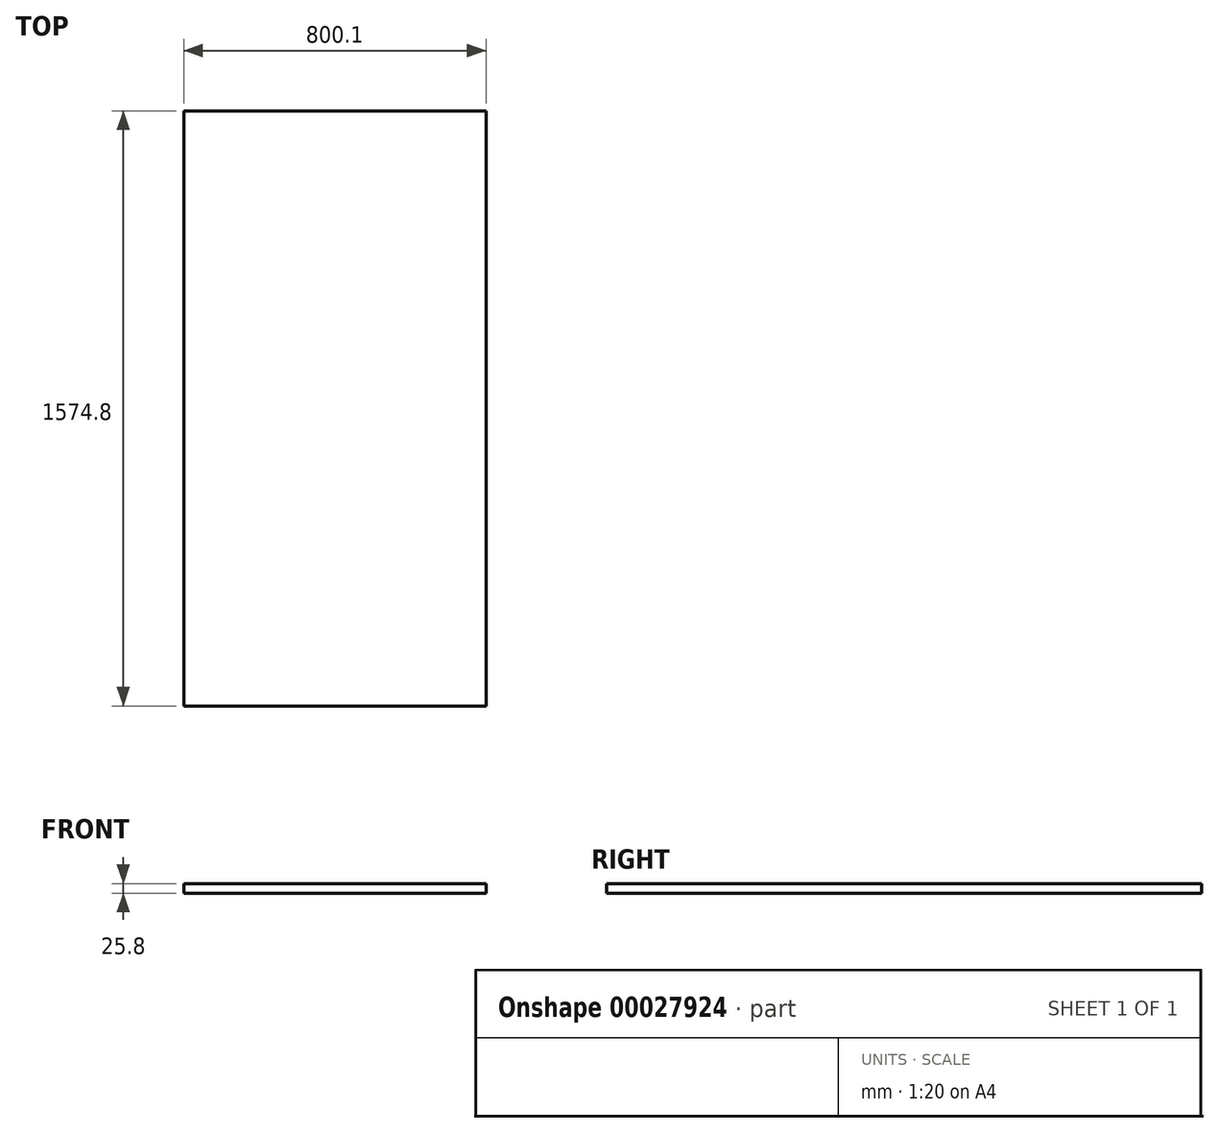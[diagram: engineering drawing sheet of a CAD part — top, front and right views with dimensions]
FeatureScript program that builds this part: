
annotation { "Feature Type Name" : "Feature", "Feature Type Description" : "" }
export const myFeature = defineFeature(function(context is Context, id is Id, definition is map)
    precondition{}
    {
        {
            var Q0;
            Q0=qCreatedBy(makeId("Front.planeOp"),FACE);
            var sketch = newSketch(context, id + "F0", { "sketchPlane" : qUnion([Q0])});
            skLineSegment(sketch, "E0", {"start": v(0, 0) * mm, "end": v(800.1, 0) * mm});
            skLineSegment(sketch, "E1", {"start": v(800.1, 0) * mm, "end": v(800.1, 25.8) * mm});
            skLineSegment(sketch, "E2", {"start": v(800.1, 25.8) * mm, "end": v(0, 25.8) * mm});
            skLineSegment(sketch, "E3", {"start": v(0, 25.8) * mm, "end": v(0, 0) * mm});
            skSolve(sketch);
        }
        {
            var Q0;
            Q0=qSketchRegion(id+"F0",true);
            extrude(context, id + "F1", {"entities" : qUnion([Q0]), "depth" : 1574.8 * mm});
        }
    });
